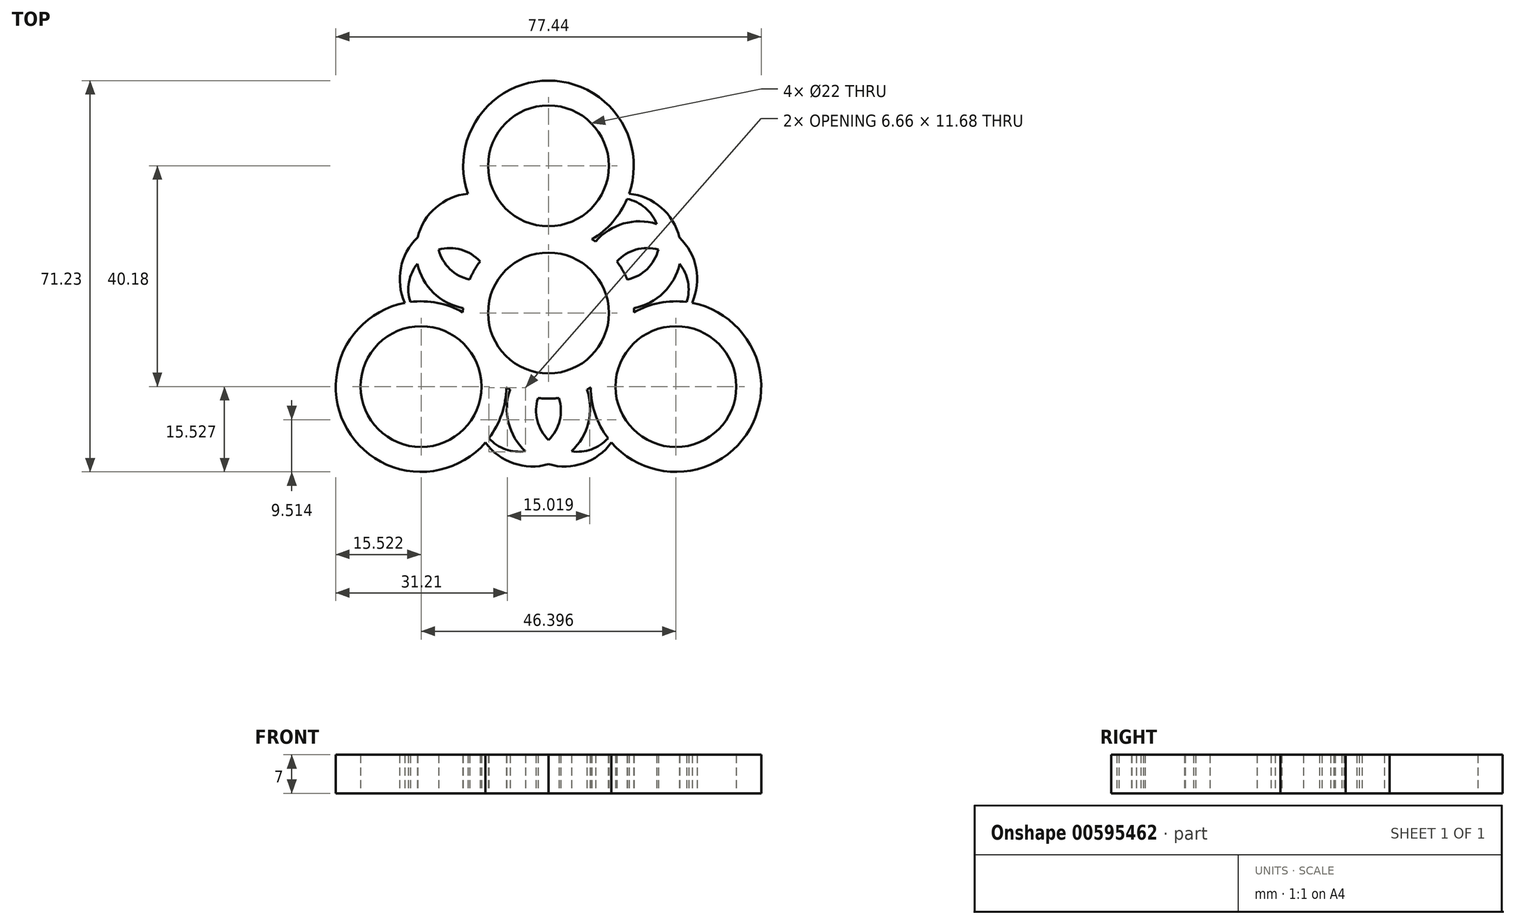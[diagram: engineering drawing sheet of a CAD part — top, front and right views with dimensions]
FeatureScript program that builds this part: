
annotation { "Feature Type Name" : "Feature", "Feature Type Description" : "" }
export const myFeature = defineFeature(function(context is Context, id is Id, definition is map)
    precondition{}
    {
        {
            var Q0;
            Q0=qCreatedBy(makeId("Top.planeOp"),FACE);
            var sketch = newSketch(context, id + "F0", { "sketchPlane" : qUnion([Q0])});
            skCircle(sketch, "E0", {"center": v(0, 0) * mm, "radius": 11 * mm});
            skCircle(sketch, "E1", {"center": v(0, 26.79) * mm, "radius": 11 * mm});
            skArc(sketch, "E2", {"start": v(7.9, 13.43) * mm, "mid": v(0, 42.3) * mm, "end": v(-7.9, 13.43) * mm});
            skArc(sketch, "E3", {"start": v(-7.68, -13.56) * mm, "mid": v(-7.34, -13.75) * mm, "end": v(-7, -13.93) * mm});
            skCircle(sketch, "E4.1.0", {"center": v(-23.2, -13.4) * mm, "radius": 11 * mm});
            skCircle(sketch, "E4.2.0", {"center": v(23.2, -13.4) * mm, "radius": 11 * mm});
            skArc(sketch, "E5.1.0", {"start": v(-15.59, 0.13) * mm, "mid": v(-36.64, -21.15) * mm, "end": v(-7.68, -13.56) * mm});
            skArc(sketch, "E5.2.0", {"start": v(7.68, -13.56) * mm, "mid": v(36.64, -21.15) * mm, "end": v(15.59, 0.13) * mm});
            skArc(sketch, "E6.trimOffspring", {"start": v(15.59, 0.13) * mm, "mid": v(15.58, 0.52) * mm, "end": v(15.56, 0.9) * mm});
            skArc(sketch, "E7.trimOffspring", {"start": v(-7.9, 13.43) * mm, "mid": v(-8.24, 13.23) * mm, "end": v(-8.57, 13.02) * mm});
            skArc(sketch, "E8", {"start": v(14.35, 6.07) * mm, "mid": v(17.95, 8.02) * mm, "end": v(20, 11.55) * mm});
            skArc(sketch, "E9", {"start": v(15.56, 0.9) * mm, "mid": v(20.93, 3.69) * mm, "end": v(23.89, 8.97) * mm});
            skArc(sketch, "E10.1.0", {"start": v(-8.57, 13.02) * mm, "mid": v(-22.2, 15.05) * mm, "end": v(-26.14, 1.85) * mm});
            skArc(sketch, "E10.1.1", {"start": v(-12.44, 9.4) * mm, "mid": v(-15.92, 11.54) * mm, "end": v(-20, 11.55) * mm});
            skArc(sketch, "E10.2.0", {"start": v(-7, -13.93) * mm, "mid": v(-7.27, -19.97) * mm, "end": v(-4.18, -25.17) * mm});
            skArc(sketch, "E10.2.1", {"start": v(-1.92, -15.47) * mm, "mid": v(-2.03, -19.55) * mm, "end": v(0, -23.1) * mm});
            skArc(sketch, "E11.MirrorCS", {"start": v(7, -13.93) * mm, "mid": v(7.27, -19.97) * mm, "end": v(4.18, -25.17) * mm});
            skArc(sketch, "E12.MirrorCS", {"start": v(1.92, -15.47) * mm, "mid": v(2.03, -19.55) * mm, "end": v(0, -23.1) * mm});
            skArc(sketch, "E13.1.0", {"start": v(-8.57, 13.02) * mm, "mid": v(-13.66, 16.28) * mm, "end": v(-19.7, 16.2) * mm});
            skArc(sketch, "E13.1.1", {"start": v(8.57, 13.02) * mm, "mid": v(13.66, 16.28) * mm, "end": v(19.7, 16.2) * mm});
            skArc(sketch, "E13.1.2", {"start": v(12.44, 9.4) * mm, "mid": v(15.92, 11.54) * mm, "end": v(20, 11.55) * mm});
            skArc(sketch, "E13.2.1", {"start": v(-15.56, 0.9) * mm, "mid": v(-20.93, 3.69) * mm, "end": v(-23.89, 8.97) * mm});
            skArc(sketch, "E13.2.2", {"start": v(-14.35, 6.07) * mm, "mid": v(-17.95, 8.02) * mm, "end": v(-20, 11.55) * mm});
            skArc(sketch, "E14.trimOffspring", {"start": v(-23.89, 8.97) * mm, "mid": v(-25.39, 5.64) * mm, "end": v(-25.15, 2) * mm});
            skArc(sketch, "E15.trimOffspring", {"start": v(-19.7, 16.2) * mm, "mid": v(-17.58, 19.17) * mm, "end": v(-14.31, 20.78) * mm});
            skArc(sketch, "E16.trimOffspring", {"start": v(-23.83, 13.76) * mm, "mid": v(-20.52, 19.2) * mm, "end": v(-14.67, 21.72) * mm});
            skArc(sketch, "E17.trimOffspring", {"start": v(-23.83, 13.76) * mm, "mid": v(-26.88, 8.17) * mm, "end": v(-26.14, 1.85) * mm});
            skArc(sketch, "E18.trimOffspring", {"start": v(4.18, -25.17) * mm, "mid": v(7.8, -24.8) * mm, "end": v(10.84, -22.79) * mm});
            skArc(sketch, "E19.trimOffspring", {"start": v(-4.18, -25.17) * mm, "mid": v(-7.8, -24.8) * mm, "end": v(-10.84, -22.79) * mm});
            skArc(sketch, "E20.trimOffspring", {"start": v(0, -27.52) * mm, "mid": v(6.36, -27.36) * mm, "end": v(11.47, -23.56) * mm});
            skArc(sketch, "E21.trimOffspring", {"start": v(0, -27.52) * mm, "mid": v(-6.36, -27.36) * mm, "end": v(-11.47, -23.56) * mm});
            skArc(sketch, "E22.trimOffspring", {"start": v(23.89, 8.97) * mm, "mid": v(25.39, 5.64) * mm, "end": v(25.15, 2) * mm});
            skArc(sketch, "E23.trimOffspring", {"start": v(19.7, 16.2) * mm, "mid": v(17.58, 19.17) * mm, "end": v(14.31, 20.78) * mm});
            skArc(sketch, "E24.trimOffspring", {"start": v(23.83, 13.76) * mm, "mid": v(26.88, 8.17) * mm, "end": v(26.14, 1.85) * mm});
            skArc(sketch, "E25.trimOffspring", {"start": v(23.83, 13.76) * mm, "mid": v(20.52, 19.2) * mm, "end": v(14.67, 21.72) * mm});
            skArc(sketch, "E26.trimOffspring", {"start": v(14.35, 6.07) * mm, "mid": v(13.5, 7.8) * mm, "end": v(12.44, 9.4) * mm});
            skArc(sketch, "E27.trimOffspring", {"start": v(8.57, 13.02) * mm, "mid": v(8.24, 13.23) * mm, "end": v(7.9, 13.43) * mm});
            skArc(sketch, "E28.trimOffspring", {"start": v(-12.44, 9.4) * mm, "mid": v(-13.5, 7.8) * mm, "end": v(-14.35, 6.07) * mm});
            skArc(sketch, "E29.trimOffspring", {"start": v(-15.56, 0.9) * mm, "mid": v(-15.58, 0.52) * mm, "end": v(-15.59, 0.13) * mm});
            skArc(sketch, "E30.trimOffspring", {"start": v(-1.92, -15.47) * mm, "mid": v(0, -15.59) * mm, "end": v(1.92, -15.47) * mm});
            skArc(sketch, "E31.trimOffspring", {"start": v(7, -13.93) * mm, "mid": v(7.34, -13.75) * mm, "end": v(7.68, -13.56) * mm});
            skSolve(sketch);
        }
        {
            var Q0;
            Q0=makeQuery(id+"F0.imprint","IMPRINT",FACE,{"disambiguationData":[TD([[makeQuery(id+"F0.imprint","IMPRINT",EDGE,{"derivedFrom":sQuery(id+"F0.wireOp",EDGE,"E0")}),-1.0]])]});
            var Q1;
            Q1=makeQuery(id+"F0.imprint","IMPRINT",FACE,{"disambiguationData":[TD([[makeQuery(id+"F0.imprint","IMPRINT",EDGE,{"derivedFrom":sQuery(id+"F0.wireOp",EDGE,"E10.1.0")}),-1.0]])]});
            extrude(context, id + "F1", {"entities" : qUnion([Q0, Q1]), "depth" : 7 * mm, "offsetDistance" : 25 * mm});
        }
    });
